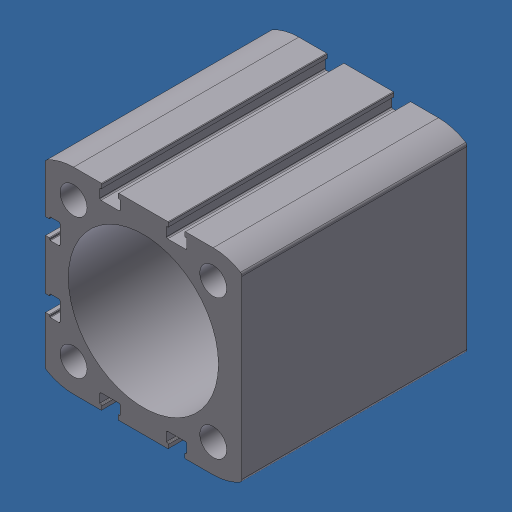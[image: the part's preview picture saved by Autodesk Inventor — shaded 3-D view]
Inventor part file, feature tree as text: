
AUTODESK INVENTOR PART (.ipt)
format: ipt  version: 2024.3 (Build 283343000, 343)  size: 317,952 bytes
history: native  units: mm (DEFAULTED — no unit token found)
features: other x1, extrude x1, hole x1, sketch x1
ambient origin geometry x8: Origin, YZ Plane, XZ Plane, XY Plane, X Axis, Y Axis, Z Axis, Center Point
bodies: Body1 (feature_tree)
feature tree (4):
  other  "Finish - None"
  extrude  "FESTO, 50MM"  Depth=0.4mm
  hole  "Hole1"  [1 undecoded]
  sketch  "Sketch1"  dims[d0=35.8mm d1=50.0mm d2=75.0mm d3=0.0mm d4=0.2mm d5=0.2mm d6=0.4mm d7=23.25mm d8=23.25mm d9=23.25mm d10=23.25mm d11=9.0mm d12=6.0mm d13=4.0mm d14=2.0mm d15=14.3117mm d16=8.0mm d17=20.594885mm]
note: 1 required parameter value undecoded (feature->parameter linkage not recoverable at this tier; creation-order binding heuristic only, values carry confidence <= 0.55)
